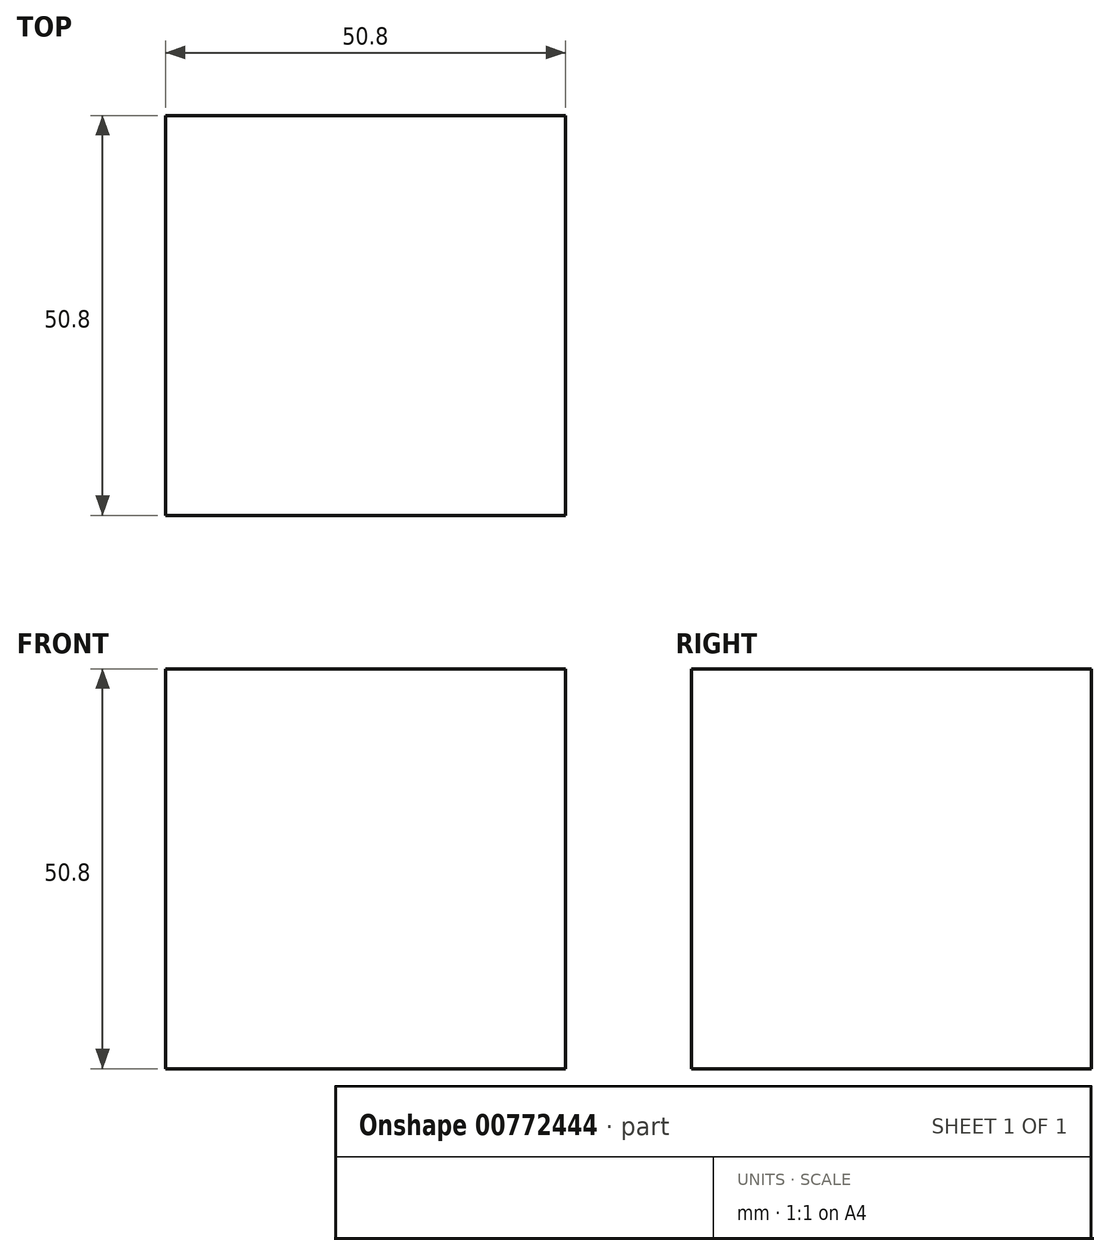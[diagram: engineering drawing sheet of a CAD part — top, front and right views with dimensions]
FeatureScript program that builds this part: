
annotation { "Feature Type Name" : "Feature", "Feature Type Description" : "" }
export const myFeature = defineFeature(function(context is Context, id is Id, definition is map)
    precondition{}
    {
        {
            var Q0;
            Q0=qCreatedBy(makeId("Front.planeOp"),FACE);
            var sketch = newSketch(context, id + "F0", { "sketchPlane" : qUnion([Q0])});
            skLineSegment(sketch, "E0.bottom", {"start": v(25.4, 25.4) * mm, "end": v(-25.4, 25.4) * mm});
            skLineSegment(sketch, "E0.top", {"start": v(25.4, -25.4) * mm, "end": v(-25.4, -25.4) * mm});
            skLineSegment(sketch, "E0.left", {"start": v(25.4, 25.4) * mm, "end": v(25.4, -25.4) * mm});
            skLineSegment(sketch, "E0.right", {"start": v(-25.4, 25.4) * mm, "end": v(-25.4, -25.4) * mm});
            skPoint(sketch, "E0.middle", {"position": v(0, 0) * mm});
            skSolve(sketch);
        }
        {
            var Q0;
            Q0=makeQuery(id+"F0.imprint","IMPRINT",FACE,{"disambiguationData":[TD([[makeQuery(id+"F0.imprint","IMPRINT",EDGE,{"derivedFrom":sQuery(id+"F0.wireOp",EDGE,"E0.bottom")}),1.0]])]});
            extrude(context, id + "F1", {"entities" : qUnion([Q0]), "depth" : 50.8 * mm, "offsetDistance" : 25.4 * mm});
        }
    });
